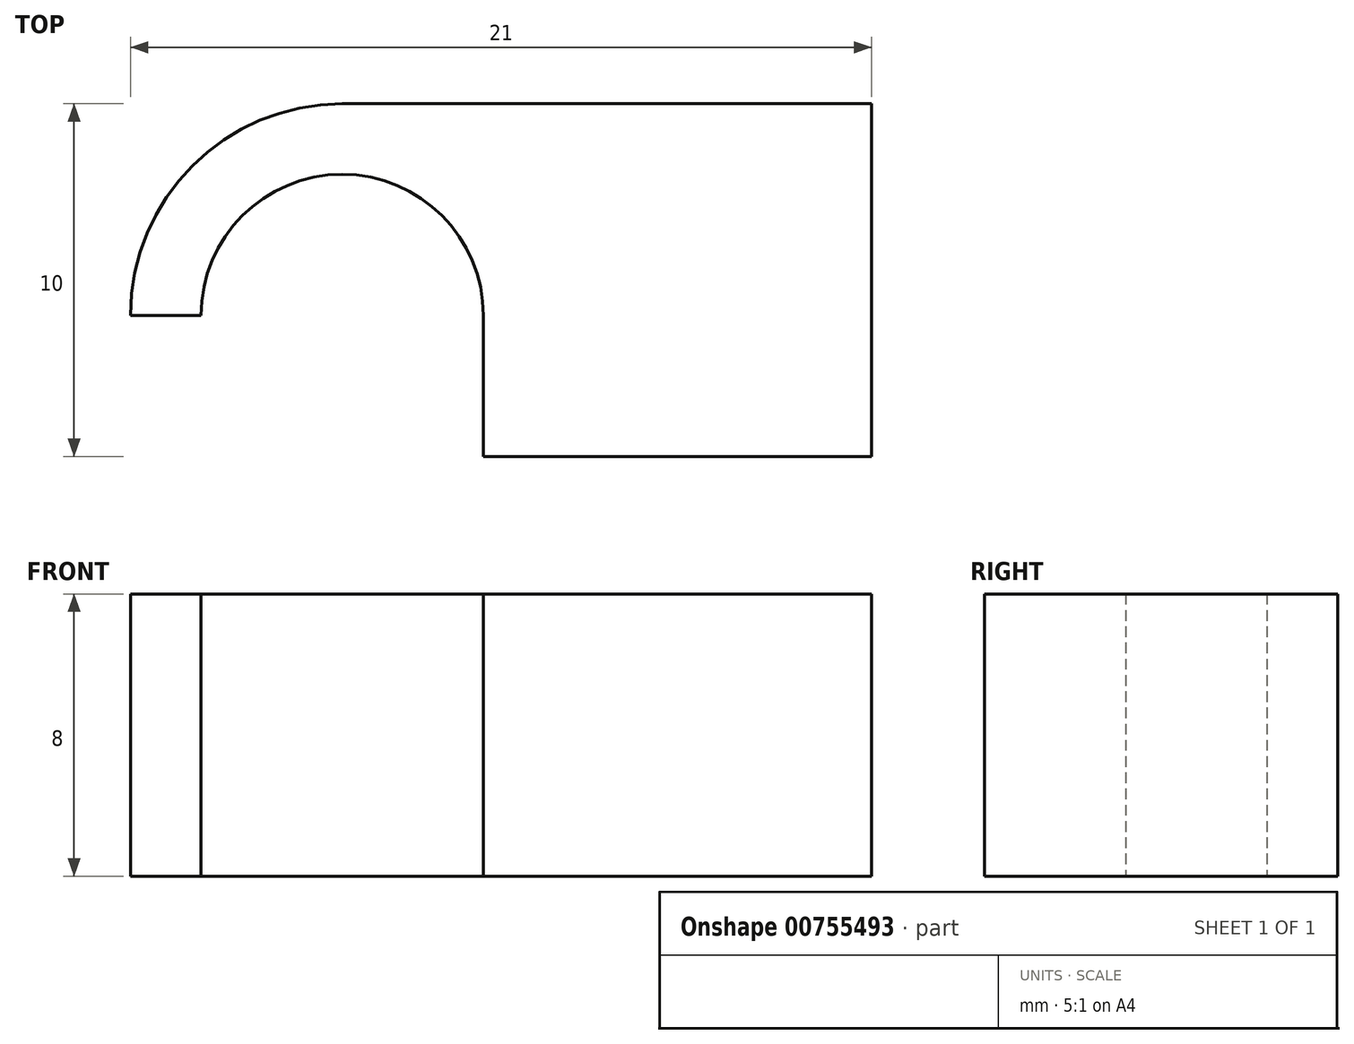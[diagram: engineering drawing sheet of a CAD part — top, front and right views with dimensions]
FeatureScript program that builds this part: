
annotation { "Feature Type Name" : "Feature", "Feature Type Description" : "" }
export const myFeature = defineFeature(function(context is Context, id is Id, definition is map)
    precondition{}
    {
        {
            var Q0;
            Q0=qCreatedBy(makeId("Top.planeOp"),FACE);
            var sketch = newSketch(context, id + "F0", { "sketchPlane" : qUnion([Q0])});
            skArc(sketch, "E0", {"start": v(4, 0) * mm, "mid": v(0, 4) * mm, "end": v(-4, 0) * mm});
            skArc(sketch, "E1.0", {"start": v(0, 6) * mm, "mid": v(-4.24, 4.24) * mm, "end": v(-6, 0) * mm});
            skLineSegment(sketch, "E2", {"start": v(0, 6) * mm, "end": v(15, 6) * mm});
            skLineSegment(sketch, "E3", {"start": v(15, 6) * mm, "end": v(15, -4) * mm});
            skLineSegment(sketch, "E4", {"start": v(4, -4) * mm, "end": v(15, -4) * mm});
            skLineSegment(sketch, "E5", {"start": v(-6, 0) * mm, "end": v(-4, 0) * mm});
            skLineSegment(sketch, "E6", {"start": v(4, 0) * mm, "end": v(4, -4) * mm});
            skPoint(sketch, "E7.orphan", {"position": v(0, -4) * mm});
            skSolve(sketch);
        }
        {
            var Q0;
            Q0=makeQuery(id+"F0.imprint","IMPRINT",FACE,{"disambiguationData":[TD([[makeQuery(id+"F0.imprint","IMPRINT",EDGE,{"derivedFrom":sQuery(id+"F0.wireOp",EDGE,"E0")}),-1.0]])]});
            extrude(context, id + "F1", {"entities" : qUnion([Q0]), "endBound" : BoundingType.SYMMETRIC, "depth" : 8 * mm, "offsetDistance" : 25 * mm});
        }
    });
